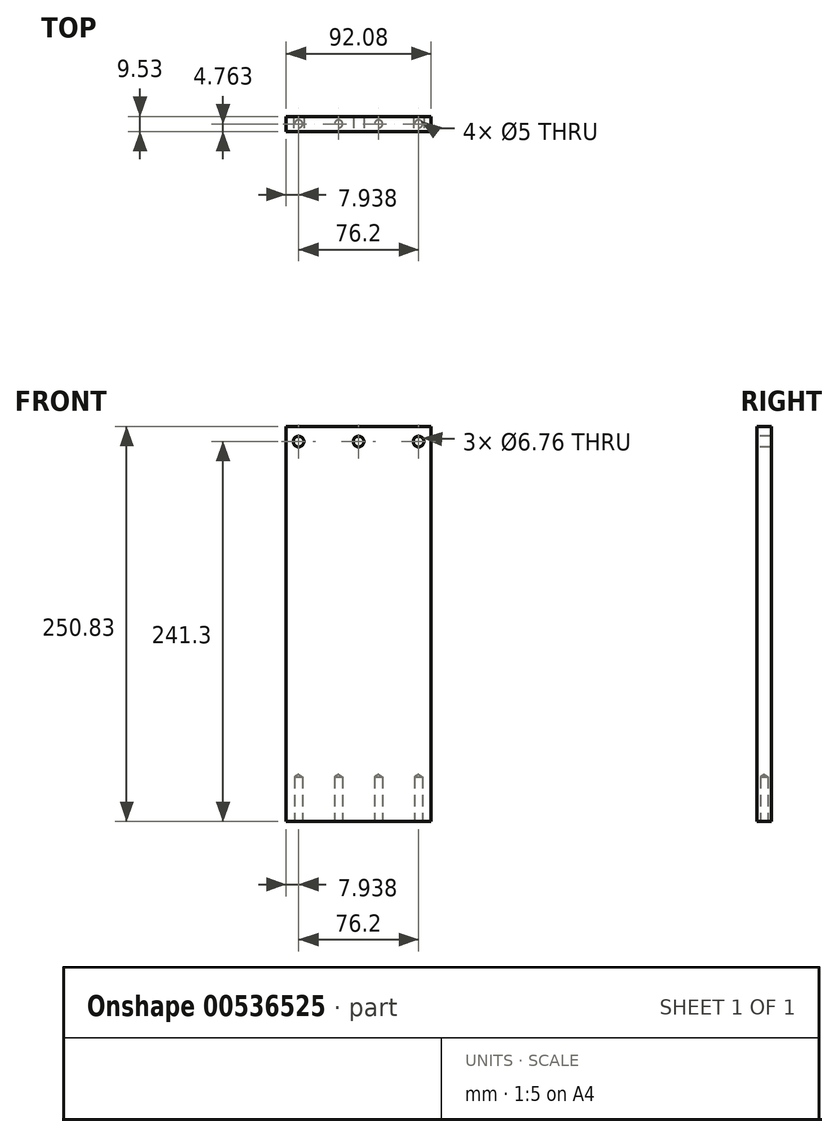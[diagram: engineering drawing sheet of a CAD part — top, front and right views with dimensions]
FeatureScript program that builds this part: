
annotation { "Feature Type Name" : "Feature", "Feature Type Description" : "" }
export const myFeature = defineFeature(function(context is Context, id is Id, definition is map)
    precondition{}
    {
        {
            var Q0;
            Q0=qCreatedBy(makeId("Front.planeOp"),FACE);
            var sketch = newSketch(context, id + "F0", { "sketchPlane" : qUnion([Q0])});
            skLineSegment(sketch, "E0", {"start": v(0, 0) * mm, "end": v(0, 250.83) * mm});
            skLineSegment(sketch, "E1", {"start": v(0, 250.83) * mm, "end": v(92.08, 250.83) * mm});
            skLineSegment(sketch, "E2", {"start": v(92.08, 250.83) * mm, "end": v(92.08, 0) * mm});
            skLineSegment(sketch, "E3", {"start": v(92.08, 0) * mm, "end": v(0, 0) * mm});
            skSolve(sketch);
        }
        {
            var Q0;
            Q0 = qSketchRegion(id + "F0", true);
            extrude(context, id + "F1", {"entities" : qUnion([Q0]), "oppositeDirection" : true, "depth" : 9.52 * mm, "offsetDistance" : 25.4 * mm});
        }
        {
            var Q0;
            Q0=makeQuery(id+"F1.opExtrude","CAP_FACE",FACE,{"disambiguationData":[OSD([sQuery(id+"F0.wireOp",EDGE,"E0"),sQuery(id+"F0.wireOp",EDGE,"E1"),sQuery(id+"F0.wireOp",EDGE,"E2"),sQuery(id+"F0.wireOp",EDGE,"VsIETvyl-KDxi-2LRg-vM0n-zHIbE8wrvZj1"),sQuery(id+"F0.wireOp",EDGE,"E3"),sQuery(id+"F0.wireOp",EDGE,"00c5acac-28a1-477b-9d2e-0848f42fd663.filletArc")])],"isStart":true});
            var sketch = newSketch(context, id + "F2", { "sketchPlane" : qUnion([Q0])});
            skLineSegment(sketch, "E4", {"start": v(7.94, 241.3) * mm, "end": v(46.04, 241.3) * mm, "construction": true});
            skLineSegment(sketch, "E5", {"start": v(46.04, 241.3) * mm, "end": v(84.14, 241.3) * mm, "construction": true});
            skLineSegment(sketch, "E6", {"start": v(46.04, 250.83) * mm, "end": v(46.04, 241.3) * mm, "construction": true});
            skSolve(sketch);
        }
        {
            var Q0;
            Q0=sQuery(id+"F2.wireOp",VERTEX,"ZkfTEy0w-nZvh-nX40-HPXd-GlfoBNCCH8EF.end");
            var Q1;
            Q1=sQuery(id+"F2.wireOp",VERTEX,"ZkfTEy0w-nZvh-nX40-HPXd-GlfoBNCCH8EF.start");
            var Q2;
            Q2=sQuery(id+"F2.wireOp",VERTEX,"td6pqOP3-WZlw-q1ZI-5exv-JsEDe0HeLW2A.start");
            var Q3;
            Q3=sQuery(id+"F2.wireOp",VERTEX,"E5.start");
            var Q4;
            Q4=sQuery(id+"F2.wireOp",VERTEX,"E5.end");
            var Q5;
            Q5=sQuery(id+"F2.wireOp",VERTEX,"E4.start");
            var Q6;
            Q6=makeQuery(id+"F1.opExtrude","SWEPT_BODY",BODY,{"disambiguationData":[OSD([sQuery(id+"F0.wireOp",EDGE,"E0"),sQuery(id+"F0.wireOp",EDGE,"E1"),sQuery(id+"F0.wireOp",EDGE,"E2"),sQuery(id+"F0.wireOp",EDGE,"VsIETvyl-KDxi-2LRg-vM0n-zHIbE8wrvZj1"),sQuery(id+"F0.wireOp",EDGE,"E3"),sQuery(id+"F0.wireOp",EDGE,"00c5acac-28a1-477b-9d2e-0848f42fd663.filletArc")])]});
            hole(context, id + "F3", {"style" : HoleStyle.SIMPLE, "endStyle" : HoleEndStyle.THROUGH, "standardTappedOrClearance" : lookupTablePath({ "standard" : "ANSI", "fit" : "Normal (ASME)", "size" : "1/4", "type" : "Clearance" }), "standardBlindInLast" : lookupTablePath({ "fit" : "Free", "standard" : "ANSI", "size" : "1/4", "type" : "Clearance" }), "holeDiameter" : 6.76 * mm, "tappedDepth" : 25.4 * mm, "tapClearance" : 3, "startFromSketch" : true, "locations" : qUnion([Q0, Q1, Q2, Q3, Q4, Q5]), "scope" : qUnion([Q6])});
        }
        {
            var Q0;
            Q0=makeQuery(id+"F1.opExtrude","SWEPT_FACE",FACE,{"disambiguationData":[OSD([sQuery(id+"F0.wireOp",EDGE,"E3")])]});
            var sketch = newSketch(context, id + "F4", { "sketchPlane" : qUnion([Q0])});
            skPoint(sketch, "E7", {"position": v(7.94, -4.76) * mm});
            skPoint(sketch, "E8.1.0.0", {"position": v(33.34, -4.76) * mm});
            skPoint(sketch, "E8.2.0.0", {"position": v(58.74, -4.76) * mm});
            skPoint(sketch, "E8.3.0.0", {"position": v(84.14, -4.76) * mm});
            skPoint(sketch, "E8.4.0.0", {"position": v(109.54, -4.76) * mm});
            skPoint(sketch, "E8.5.0.0", {"position": v(134.94, -4.76) * mm});
            skLineSegment(sketch, "E8.direction1", {"start": v(7.94, -4.76) * mm, "end": v(33.34, -4.76) * mm, "construction": true});
            skLineSegment(sketch, "E9", {"start": v(58.74, -4.76) * mm, "end": v(33.34, -4.76) * mm, "construction": true});
            skLineSegment(sketch, "E10", {"start": v(46.04, 0) * mm, "end": v(46.04, -4.76) * mm, "construction": true});
            skSolve(sketch);
        }
        {
            var Q0;
            Q0=sQuery(id+"F4.wireOp",VERTEX,"E7");
            var Q1;
            Q1=sQuery(id+"F4.wireOp",VERTEX,"E8.1.0.0");
            var Q2;
            Q2=sQuery(id+"F4.wireOp",VERTEX,"E8.2.0.0");
            var Q3;
            Q3=sQuery(id+"F4.wireOp",VERTEX,"E8.3.0.0");
            var Q4;
            Q4=sQuery(id+"F4.wireOp",VERTEX,"E8.4.0.0");
            var Q5;
            Q5=sQuery(id+"F4.wireOp",VERTEX,"E8.5.0.0");
            var Q6;
            Q6=makeQuery(id+"F1.opExtrude","SWEPT_BODY",BODY,{"disambiguationData":[OSD([sQuery(id+"F0.wireOp",EDGE,"E0"),sQuery(id+"F0.wireOp",EDGE,"E1"),sQuery(id+"F0.wireOp",EDGE,"E2"),sQuery(id+"F0.wireOp",EDGE,"VsIETvyl-KDxi-2LRg-vM0n-zHIbE8wrvZj1"),sQuery(id+"F0.wireOp",EDGE,"E3"),sQuery(id+"F0.wireOp",EDGE,"00c5acac-28a1-477b-9d2e-0848f42fd663.filletArc")])]});
            hole(context, id + "F5", {"style" : HoleStyle.SIMPLE, "endStyle" : HoleEndStyle.BLIND, "standardTappedOrClearance" : lookupTablePath({ "standard" : "ISO", "engagement" : "75%", "pitch" : "1 mm", "size" : "M6", "type" : "Tapped" }), "standardBlindInLast" : lookupTablePath({ "standard" : "ISO", "engagement" : "75%", "pitch" : "1 mm", "size" : "M6", "type" : "Tapped" }), "holeDiameter" : 5 * mm, "showTappedDepth" : true, "holeDepth" : 28.4 * mm, "tappedDepth" : 25.4 * mm, "tapClearance" : 3, "startFromSketch" : true, "locations" : qUnion([Q0, Q1, Q2, Q3, Q4, Q5]), "scope" : qUnion([Q6]), "majorDiameter" : 6 * mm});
        }
    });
